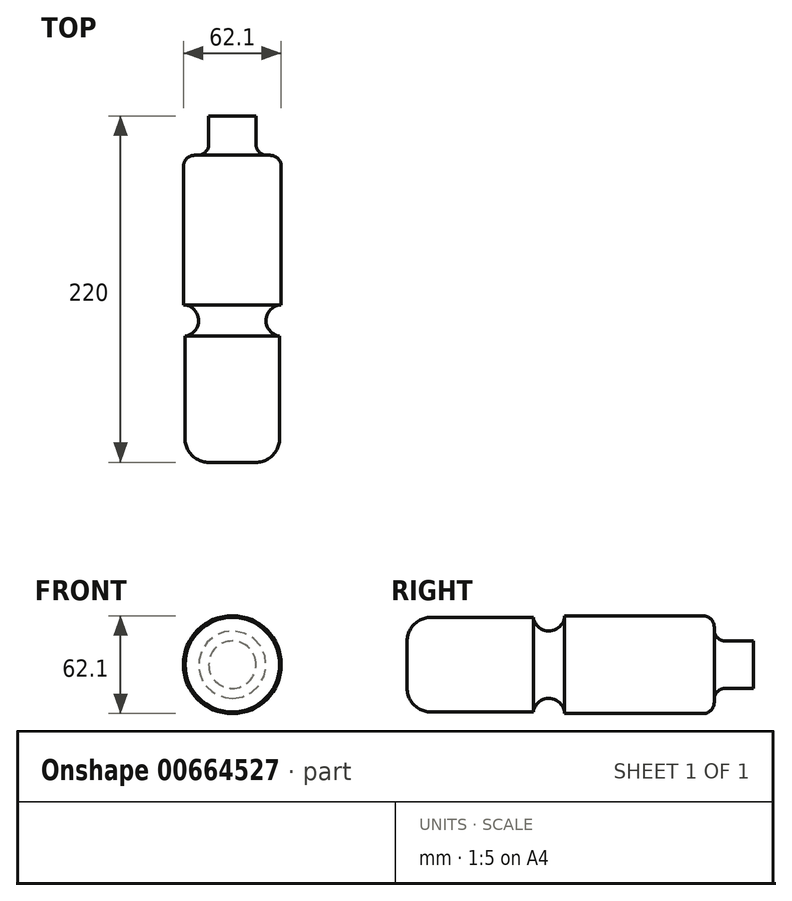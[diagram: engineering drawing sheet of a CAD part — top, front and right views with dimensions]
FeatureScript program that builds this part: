
annotation { "Feature Type Name" : "Feature", "Feature Type Description" : "" }
export const myFeature = defineFeature(function(context is Context, id is Id, definition is map)
    precondition{}
    {
        {
            var Q0;
            Q0=qCreatedBy(makeId("Right.planeOp"),FACE);
            var sketch = newSketch(context, id + "F0", { "sketchPlane" : qUnion([Q0])});
            skLineSegment(sketch, "E0", {"start": v(-123.77, 0) * mm, "end": v(276.23, 0) * mm, "construction": true});
            skLineSegment(sketch, "E1", {"start": v(-123.77, 0) * mm, "end": v(-123.77, 15) * mm});
            skLineSegment(sketch, "E2", {"start": v(-108.77, 30) * mm, "end": v(-43.68, 30) * mm});
            skLineSegment(sketch, "E3", {"start": v(-23.78, 31.05) * mm, "end": v(64.23, 31.05) * mm});
            skLineSegment(sketch, "E4", {"start": v(71.23, 24.05) * mm, "end": v(71.23, 22) * mm});
            skLineSegment(sketch, "E5", {"start": v(78.23, 15) * mm, "end": v(96.23, 15) * mm});
            skLineSegment(sketch, "E6", {"start": v(96.23, 15) * mm, "end": v(96.23, 0) * mm});
            skLineSegment(sketch, "E7", {"start": v(96.23, 0) * mm, "end": v(-123.77, 0) * mm});
            skArc(sketch, "E8", {"start": v(-43.68, 30) * mm, "mid": v(-33.25, 21.4) * mm, "end": v(-23.78, 31.05) * mm});
            skPoint(sketch, "E9.visualSharp", {"position": v(-123.77, 30) * mm});
            skArc(sketch, "E9.filletArc", {"start": v(-108.77, 30) * mm, "mid": v(-119.38, 25.6) * mm, "end": v(-123.77, 15) * mm});
            skPoint(sketch, "E10.visualSharp", {"position": v(71.23, 15) * mm});
            skArc(sketch, "E10.filletArc", {"start": v(71.23, 22) * mm, "mid": v(73.28, 17.05) * mm, "end": v(78.23, 15) * mm});
            skPoint(sketch, "E11.visualSharp", {"position": v(71.23, 31.05) * mm});
            skArc(sketch, "E11.filletArc", {"start": v(71.23, 24.05) * mm, "mid": v(69.18, 29) * mm, "end": v(64.23, 31.05) * mm});
            skSolve(sketch);
        }
        {
            var Q0;
            Q0=qSketchRegion(id+"F0",true);
            var Q1;
            Q1=sQuery(id+"F0.wireOp",EDGE,"E0");
            revolve(context, id + "F1", {"entities" : qUnion([Q0]), "axis" : qUnion([Q1]), "revolveType" : RevolveType.FULL});
        }
    });
